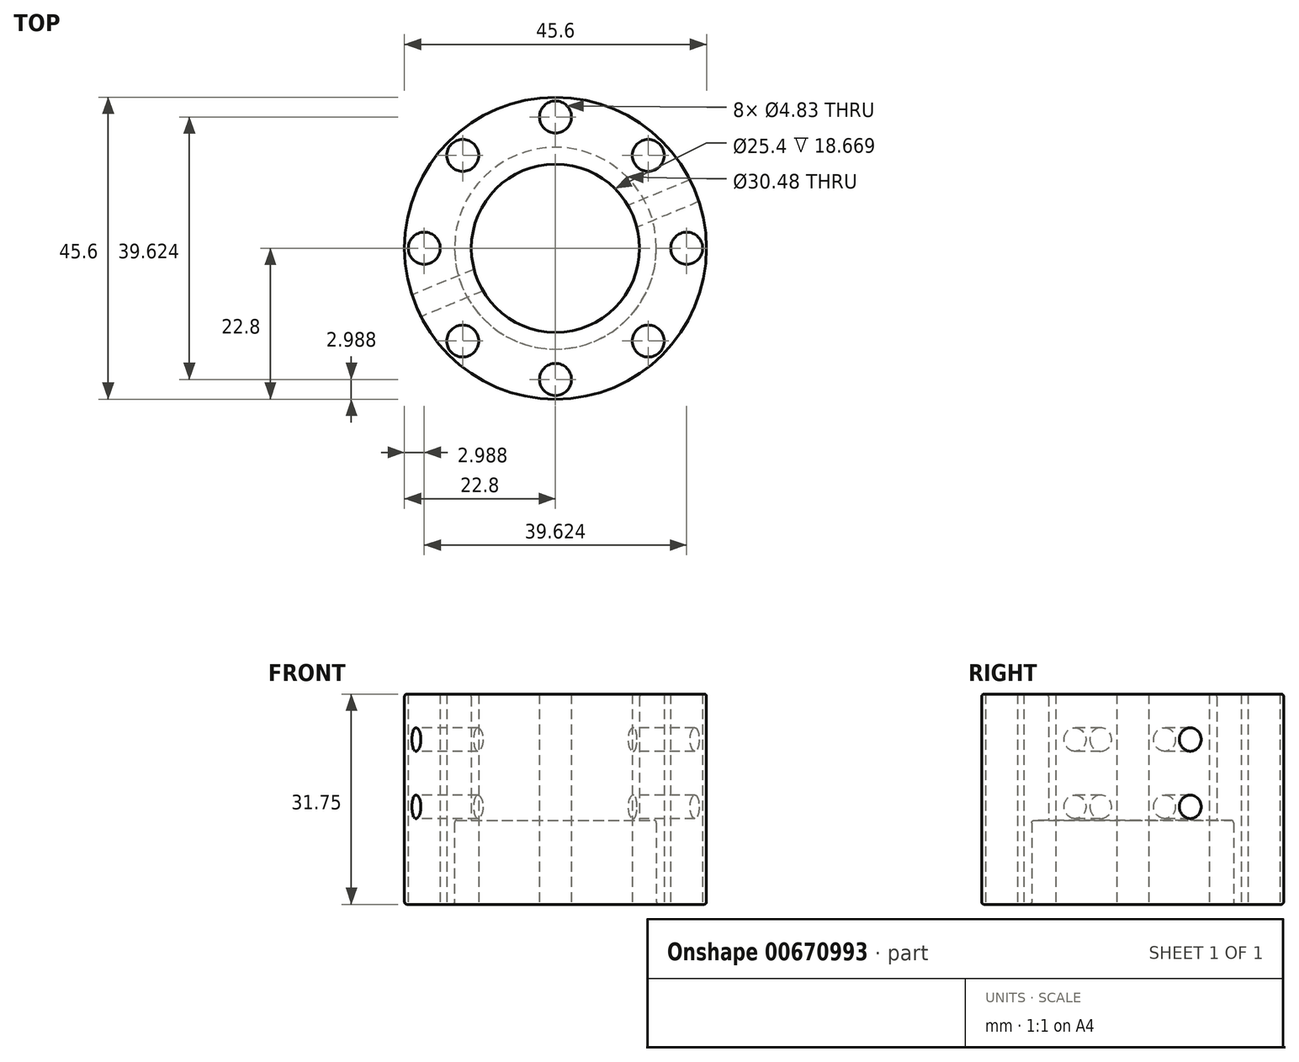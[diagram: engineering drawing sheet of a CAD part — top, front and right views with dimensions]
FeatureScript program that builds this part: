
annotation { "Feature Type Name" : "Feature", "Feature Type Description" : "" }
export const myFeature = defineFeature(function(context is Context, id is Id, definition is map)
    precondition{}
    {
        {
            var Q0;
            Q0=qCreatedBy(makeId("Top.planeOp"),FACE);
            var sketch = newSketch(context, id + "F0", { "sketchPlane" : qUnion([Q0])});
            skCircle(sketch, "E0", {"center": v(0, 0) * mm, "radius": 22.8 * mm});
            skSolve(sketch);
        }
        {
            var Q0;
            Q0 = qSketchRegion(id + "F0", true);
            extrude(context, id + "F1", {"entities" : qUnion([Q0]), "depth" : 31.75 * mm, "offsetDistance" : 25.4 * mm});
        }
        {
            var Q0;
            Q0=makeQuery(id+"F1.opExtrude","CAP_FACE",FACE,{"disambiguationData":[OSD([sQuery(id+"F0.wireOp",EDGE,"E0")])],"isStart":true});
            var sketch = newSketch(context, id + "F2", { "sketchPlane" : qUnion([Q0])});
            skCircle(sketch, "E1", {"center": v(0, 0) * mm, "radius": 15.24 * mm});
            skSolve(sketch);
        }
        {
            var Q0;
            Q0 = qSketchRegion(id + "F2", true);
            extrude(context, id + "F3", {"entities" : qUnion([Q0]), "operationType" : NewBodyOperationType.REMOVE, "oppositeDirection" : true, "depth" : 12.7 * mm, "offsetDistance" : 25.4 * mm});
        }
        {
            var Q0;
            Q0=makeQuery(id+"F3.boolean.opBoolean","COPY",FACE,{"derivedFrom":makeQuery(id+"F3.opExtrude","CAP_FACE",FACE,{"disambiguationData":[OSD([sQuery(id+"F2.wireOp",EDGE,"E1")])],"isStart":false})});
            var sketch = newSketch(context, id + "F4", { "sketchPlane" : qUnion([Q0])});
            skCircle(sketch, "E2", {"center": v(0, 0) * mm, "radius": 12.7 * mm});
            skSolve(sketch);
        }
        {
            var Q0;
            Q0 = qSketchRegion(id + "F4", true);
            extrude(context, id + "F5", {"entities" : qUnion([Q0]), "operationType" : NewBodyOperationType.REMOVE, "endBound" : BoundingType.THROUGH_ALL, "oppositeDirection" : true, "depth" : 25.4 * mm, "offsetDistance" : 25.4 * mm});
        }
        {
            var Q0;
            Q0=makeQuery(id+"F1.opExtrude","CAP_FACE",FACE,{"disambiguationData":[OSD([sQuery(id+"F0.wireOp",EDGE,"E0")])],"isStart":false});
            var Q1;
            Q1=makeQuery(id+"F1.opExtrude","CAP_FACE",FACE,{"disambiguationData":[OSD([sQuery(id+"F0.wireOp",EDGE,"E0")])],"isStart":true});
            var Q2;
            Q2=makeQuery(id+"F5.boolean.opBoolean","COPY",EDGE,{"derivedFrom":makeQuery(id+"F5.opExtrude","CAP_EDGE",EDGE,{"disambiguationData":[OSD([sQuery(id+"F4.wireOp",EDGE,"E2")])],"isStart":true})});
            var Q3;
            Q3=makeQuery(id+"F3.boolean.opBoolean","COPY",EDGE,{"derivedFrom":makeQuery(id+"F3.opExtrude","CAP_EDGE",EDGE,{"disambiguationData":[OSD([sQuery(id+"F2.wireOp",EDGE,"E1")])],"isStart":false})});
            fillet(context, id + "F6", {"entities" : qUnion([Q0, Q1, Q2, Q3]), "radius" : 0.38 * mm, "tangentPropagation" : true, "allowEdgeOverflow" : false});
        }
        {
            var Q0;
            Q0=qCreatedBy(makeId("Right.planeOp"),FACE);
            var sketch = newSketch(context, id + "F7", { "sketchPlane" : qUnion([Q0])});
            skLineSegment(sketch, "E3", {"start": v(0, -1.99) * mm, "end": v(0, 51.01) * mm, "construction": true});
            skSolve(sketch);
        }
        {
            var Q0;
            Q0=makeQuery(id+"F1.opExtrude","CAP_FACE",FACE,{"disambiguationData":[OSD([sQuery(id+"F0.wireOp",EDGE,"E0")])],"isStart":true});
            var sketch = newSketch(context, id + "F8", { "sketchPlane" : qUnion([Q0])});
            skCircle(sketch, "E4", {"center": v(0, 19.81) * mm, "radius": 2.41 * mm});
            skCircle(sketch, "E5.1.0", {"center": v(-14, 14) * mm, "radius": 2.41 * mm});
            skCircle(sketch, "E5.2.0", {"center": v(-19.81, 0) * mm, "radius": 2.41 * mm});
            skPoint(sketch, "E5.center", {"position": v(0, 0) * mm});
            skCircle(sketch, "E6.1.3.0", {"center": v(-14, -14) * mm, "radius": 2.41 * mm});
            skCircle(sketch, "E6.1.4.0", {"center": v(0, -19.81) * mm, "radius": 2.41 * mm});
            skCircle(sketch, "E6.1.5.0", {"center": v(14, -14) * mm, "radius": 2.41 * mm});
            skCircle(sketch, "E6.1.6.0", {"center": v(19.81, 0) * mm, "radius": 2.41 * mm});
            skCircle(sketch, "E6.1.7.0", {"center": v(14, 14) * mm, "radius": 2.41 * mm});
            skSolve(sketch);
        }
        {
            var Q0;
            Q0 = qSketchRegion(id + "F8", true);
            extrude(context, id + "F9", {"entities" : qUnion([Q0]), "operationType" : NewBodyOperationType.REMOVE, "endBound" : BoundingType.THROUGH_ALL, "oppositeDirection" : true, "depth" : 25.4 * mm, "offsetDistance" : 25.4 * mm});
        }
        {
            var Q0;
            Q0=sQuery(id+"F7.wireOp",EDGE,"E3");
            cPlane(context, id + "F10", {"entities" : qUnion([Q0]), "cplaneType" : CPlaneType.LINE_ANGLE, "offset" : 17.02 * mm, "angle" : 22.5 * degree, "width" : 152.4 * mm, "height" : 152.4 * mm});
        }
        {
            var Q0;
            Q0=qCreatedBy(id+"F10.planeOp",FACE);
            var sketch = newSketch(context, id + "F11", { "sketchPlane" : qUnion([Q0])});
            skCircle(sketch, "E7", {"center": v(0, 24.9) * mm, "radius": 1.78 * mm});
            skCircle(sketch, "E8", {"center": v(0, 14.73) * mm, "radius": 1.78 * mm});
            skSolve(sketch);
        }
        {
            var Q0;
            Q0 = qSketchRegion(id + "F11", true);
            extrude(context, id + "F12", {"entities" : qUnion([Q0]), "operationType" : NewBodyOperationType.REMOVE, "endBound" : BoundingType.SYMMETRIC, "depth" : 76.2 * mm, "offsetDistance" : 25.4 * mm});
        }
    });
